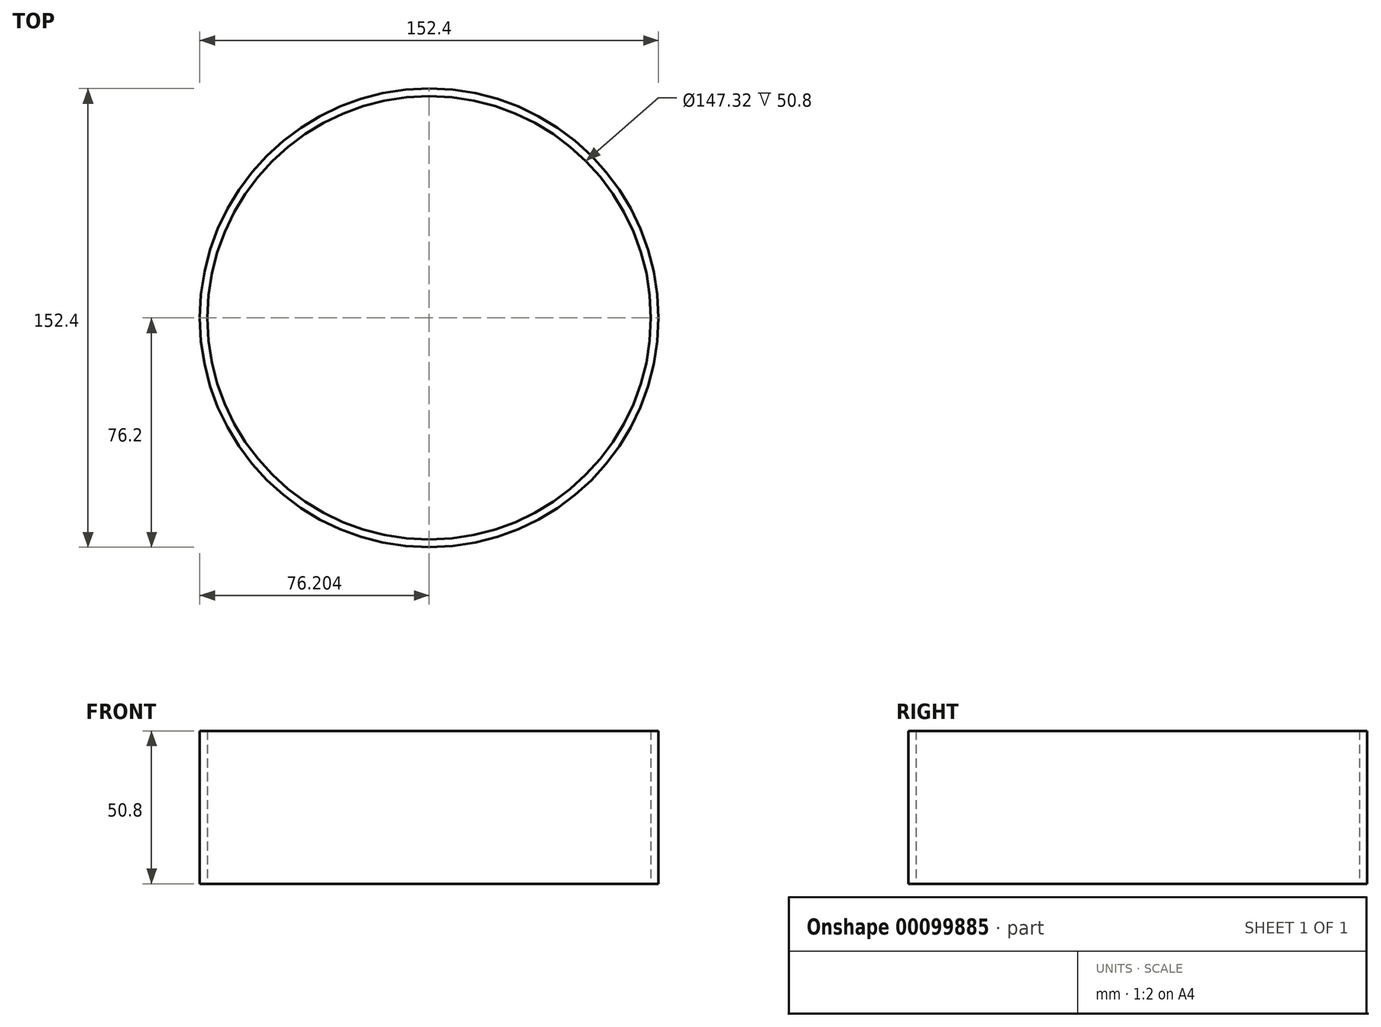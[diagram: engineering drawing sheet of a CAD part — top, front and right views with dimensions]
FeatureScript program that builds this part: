
annotation { "Feature Type Name" : "Feature", "Feature Type Description" : "" }
export const myFeature = defineFeature(function(context is Context, id is Id, definition is map)
    precondition{}
    {
        {
            var Q0;
            Q0=qCreatedBy(makeId("Top.planeOp"),FACE);
            var sketch = newSketch(context, id + "F0", { "sketchPlane" : qUnion([Q0])});
            skCircle(sketch, "E0", {"center": v(1.3, 0) * mm, "radius": 76.2 * mm});
            skSolve(sketch);
        }
        {
            var Q0;
            Q0 = qSketchRegion(id + "F0", true);
            extrude(context, id + "F1", {"entities" : qUnion([Q0]), "depth" : 25.4 * mm, "hasSecondDirection" : true, "secondDirectionOppositeDirection" : true, "secondDirectionDepth" : 25.4 * mm});
        }
        {
            var Q0;
            Q0=makeQuery(id+"F1.opExtrude","CAP_FACE",FACE,{"disambiguationData":[OSD([sQuery(id+"F0.wireOp",EDGE,"E0")])],"isStart":false});
            var Q1;
            Q1=makeQuery(id+"F1.opExtrude","CAP_FACE",FACE,{"disambiguationData":[OSD([sQuery(id+"F0.wireOp",EDGE,"E0")])],"isStart":true});
            shell(context, id + "F2", {"entities" : qUnion([Q0, Q1]), "thickness" : 2.54 * mm});
        }
    });
